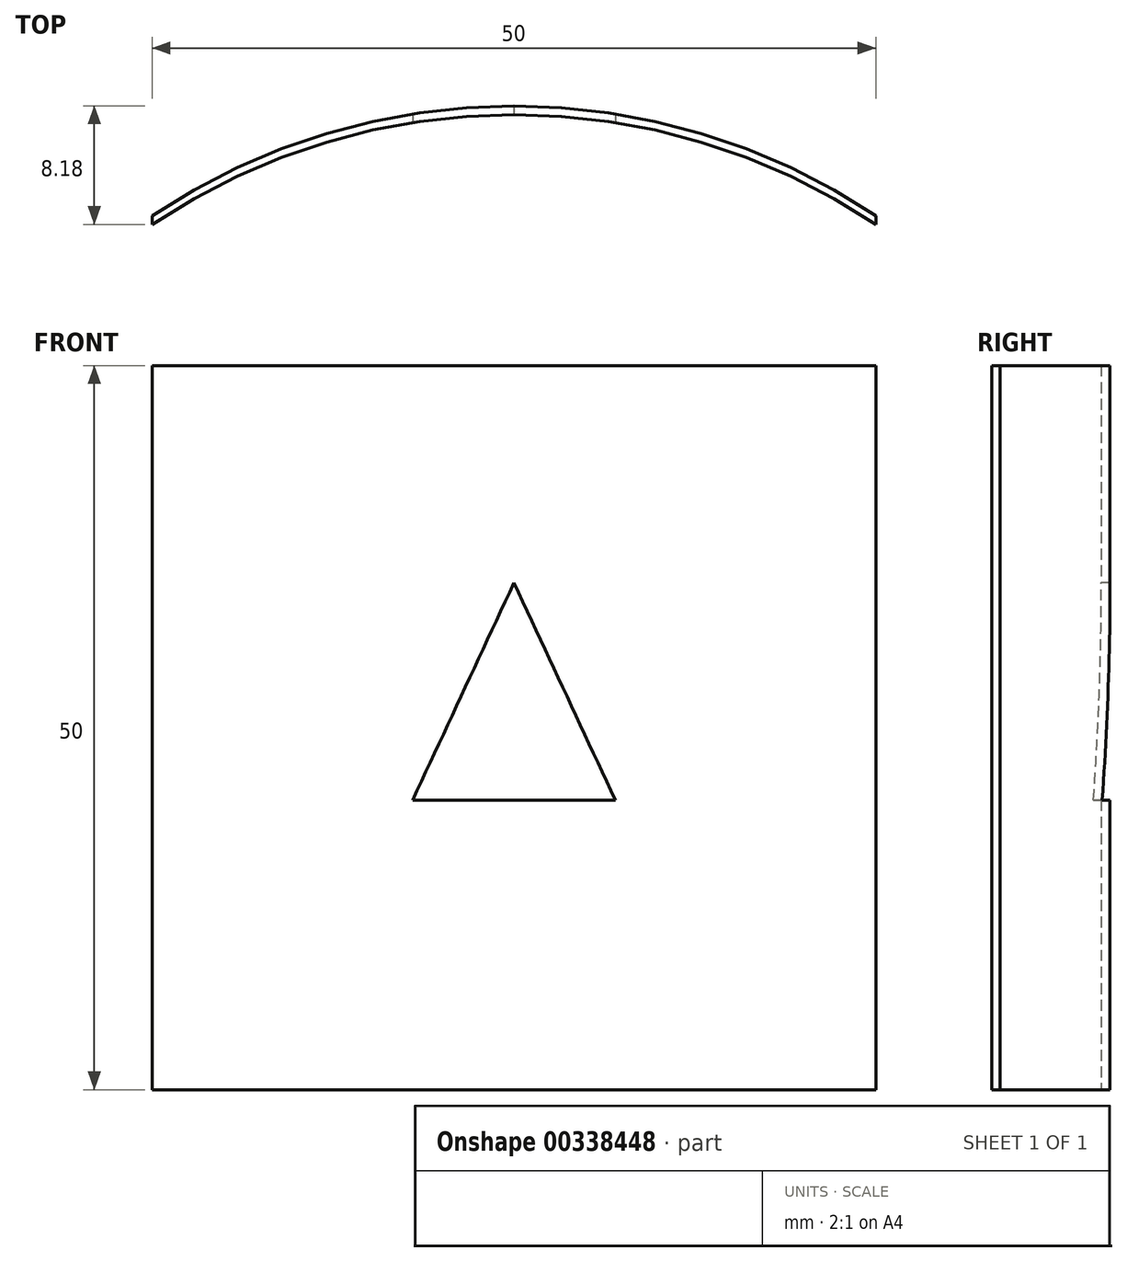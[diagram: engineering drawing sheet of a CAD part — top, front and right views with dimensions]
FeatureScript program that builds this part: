
annotation { "Feature Type Name" : "Feature", "Feature Type Description" : "" }
export const myFeature = defineFeature(function(context is Context, id is Id, definition is map)
    precondition{}
    {
        {
            var Q0;
            Q0=qCreatedBy(makeId("Top.planeOp"),FACE);
            var sketch = newSketch(context, id + "F0", { "sketchPlane" : qUnion([Q0])});
            skArc(sketch, "E0", {"start": v(50, 0) * mm, "mid": v(25, 7.58) * mm, "end": v(0, 0) * mm});
            skLineSegment(sketch, "E1", {"start": v(0, 0) * mm, "end": v(0, 0.6) * mm});
            skLineSegment(sketch, "E2", {"start": v(50, 0) * mm, "end": v(50, 0.6) * mm});
            skArc(sketch, "E3", {"start": v(50, 0.6) * mm, "mid": v(25, 8.18) * mm, "end": v(0, 0.6) * mm});
            skSolve(sketch);
        }
        {
            var Q0;
            Q0=makeQuery(id+"F0.imprint","IMPRINT",FACE,{"disambiguationData":[TD([[makeQuery(id+"F0.imprint","IMPRINT",EDGE,{"derivedFrom":sQuery(id+"F0.wireOp",EDGE,"E0")}),-1.0]])]});
            extrude(context, id + "F1", {"entities" : qUnion([Q0]), "depth" : 50 * mm});
        }
        {
            var Q0;
            Q0=qCreatedBy(makeId("Front.planeOp"),FACE);
            var sketch = newSketch(context, id + "F2", { "sketchPlane" : qUnion([Q0])});
            skLineSegment(sketch, "E4.0.0", {"start": v(0, 0) * mm, "end": v(50, 0) * mm});
            skLineSegment(sketch, "E4.0.1", {"start": v(50, 0) * mm, "end": v(50, 50) * mm});
            skLineSegment(sketch, "E4.0.2", {"start": v(50, 50) * mm, "end": v(0, 50) * mm});
            skLineSegment(sketch, "E4.0.3", {"start": v(0, 50) * mm, "end": v(0, 0) * mm});
            skLineSegment(sketch, "E5", {"start": v(18, 20) * mm, "end": v(32, 20) * mm});
            skLineSegment(sketch, "E6", {"start": v(32, 20) * mm, "end": v(25, 35) * mm});
            skLineSegment(sketch, "E7", {"start": v(25, 35) * mm, "end": v(18, 20) * mm});
            skSolve(sketch);
        }
        {
            var Q0;
            Q0=makeQuery(id+"F2.imprint","IMPRINT",FACE,{"disambiguationData":[TD([[makeQuery(id+"F2.imprint","IMPRINT",EDGE,{"derivedFrom":sQuery(id+"F2.wireOp",EDGE,"E5")}),1.0]])]});
            extrude(context, id + "F3", {"entities" : qUnion([Q0]), "operationType" : NewBodyOperationType.REMOVE, "oppositeDirection" : true, "depth" : 25 * mm});
        }
    });
